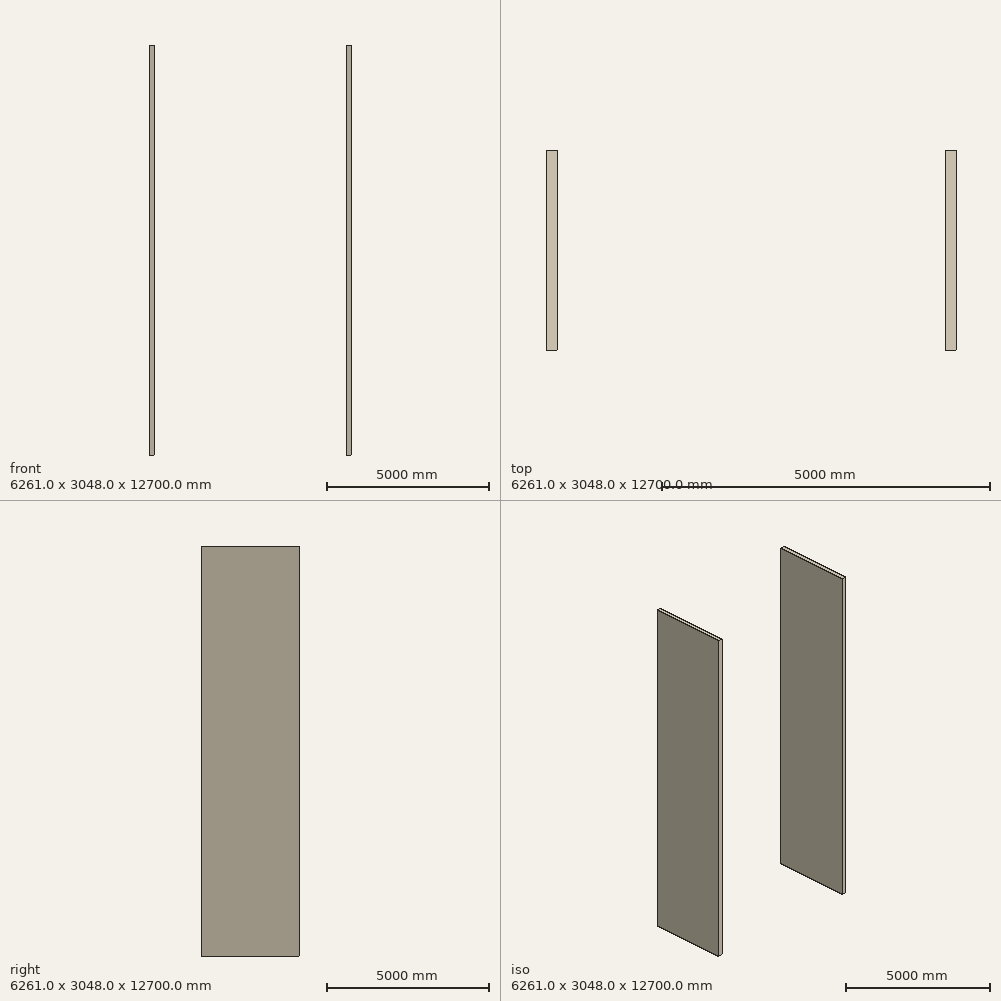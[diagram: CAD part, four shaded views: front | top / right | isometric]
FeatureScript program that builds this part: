
annotation { "Feature Type Name" : "Feature", "Feature Type Description" : "" }
export const myFeature = defineFeature(function(context is Context, id is Id, definition is map)
    precondition{}
    {
        {
            var Q0;
            Q0=qCreatedBy(makeId("Front.planeOp"),FACE);
            var sketch = newSketch(context, id + "F0", { "sketchPlane" : qUnion([Q0])});
            skLineSegment(sketch, "E0", {"start": v(-3048, 0) * mm, "end": v(3048, 0) * mm, "construction": true});
            skLineSegment(sketch, "E1.bottom", {"start": v(-2965.51, 0) * mm, "end": v(-3130.49, 0) * mm});
            skLineSegment(sketch, "E1.top", {"start": v(-2965.51, 12700) * mm, "end": v(-3130.49, 12700) * mm});
            skLineSegment(sketch, "E1.left", {"start": v(-2965.51, 0) * mm, "end": v(-2965.51, 12700) * mm});
            skLineSegment(sketch, "E1.right", {"start": v(-3130.49, 0) * mm, "end": v(-3130.49, 12700) * mm});
            skLineSegment(sketch, "E2.bottom", {"start": v(2965.51, 0) * mm, "end": v(3130.49, 0) * mm});
            skLineSegment(sketch, "E2.top", {"start": v(2965.51, 12700) * mm, "end": v(3130.49, 12700) * mm});
            skLineSegment(sketch, "E2.left", {"start": v(2965.51, 0) * mm, "end": v(2965.51, 12700) * mm});
            skLineSegment(sketch, "E2.right", {"start": v(3130.49, 0) * mm, "end": v(3130.49, 12700) * mm});
            skSolve(sketch);
        }
        {
            var Q0;
            Q0=makeQuery(id+"F0.imprint","IMPRINT",FACE,{"disambiguationData":[TD([[makeQuery(id+"F0.imprint","IMPRINT",EDGE,{"derivedFrom":sQuery(id+"F0.wireOp",EDGE,"E1.bottom")}),-1.0]])]});
            var Q1;
            Q1=makeQuery(id+"F0.imprint","IMPRINT",FACE,{"disambiguationData":[TD([[makeQuery(id+"F0.imprint","IMPRINT",EDGE,{"derivedFrom":sQuery(id+"F0.wireOp",EDGE,"E2.bottom")}),1.0]])]});
            extrude(context, id + "F1", {"entities" : qUnion([Q0, Q1]), "depth" : 3048 * mm, "offsetDistance" : 25.4 * mm});
        }
    });
